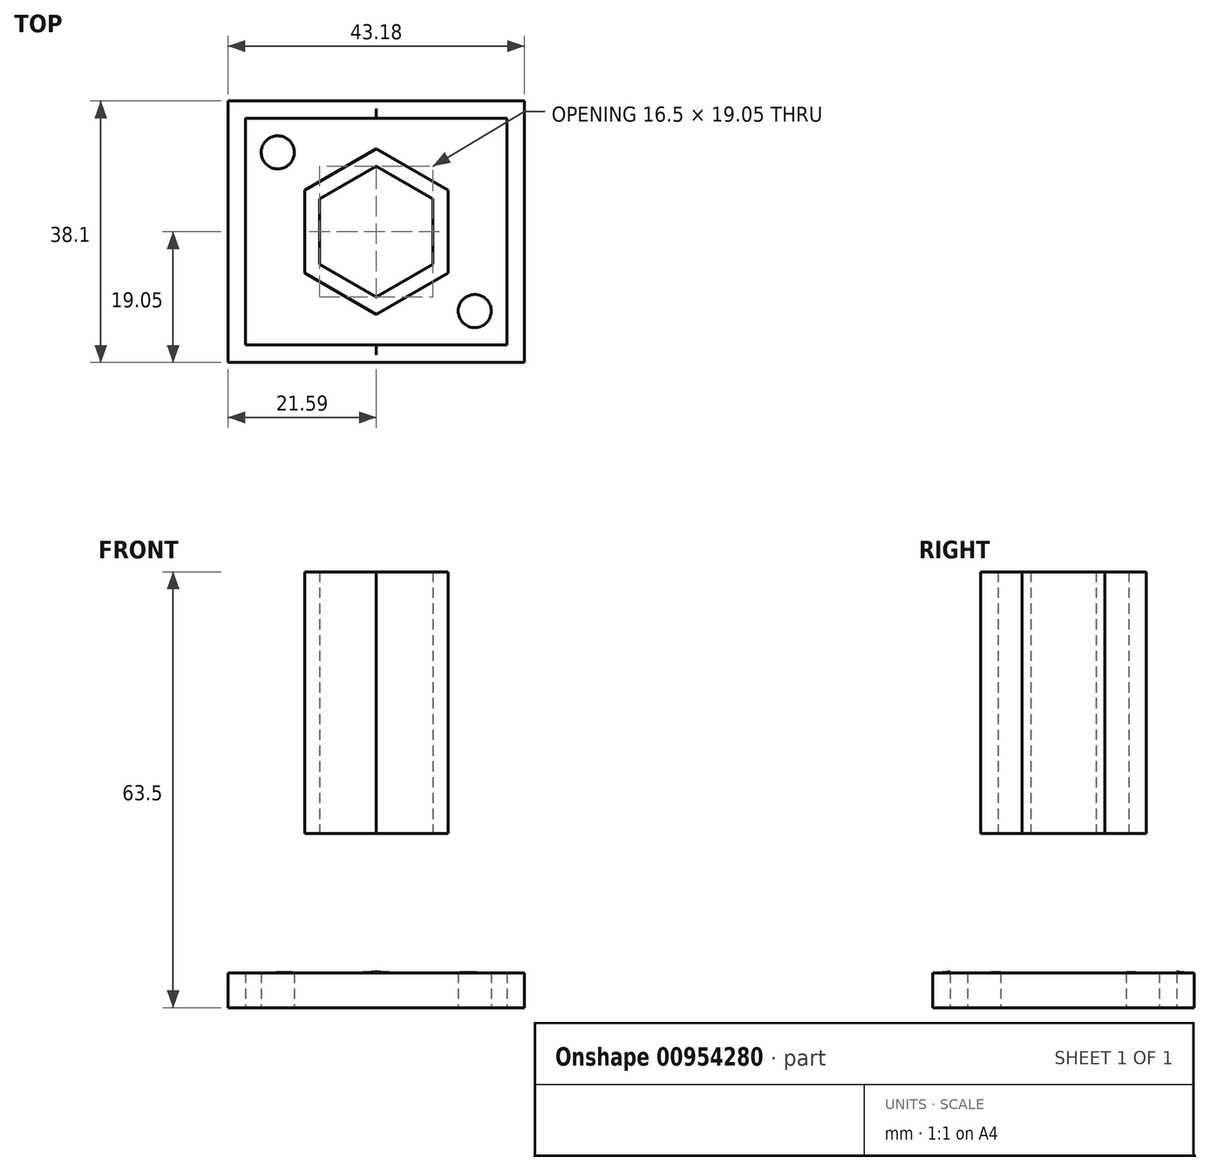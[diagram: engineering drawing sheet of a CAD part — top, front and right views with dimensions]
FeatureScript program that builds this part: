
annotation { "Feature Type Name" : "Feature", "Feature Type Description" : "" }
export const myFeature = defineFeature(function(context is Context, id is Id, definition is map)
    precondition{}
    {
        {
            var Q0;
            Q0=qCreatedBy(makeId("Front.planeOp"),FACE);
            var sketch = newSketch(context, id + "F0", { "sketchPlane" : qUnion([Q0])});
            skLineSegment(sketch, "E0.bottom", {"start": v(-21.59, -11.25) * mm, "end": v(21.59, -11.25) * mm});
            skLineSegment(sketch, "E0.top", {"start": v(-21.59, -16.33) * mm, "end": v(21.59, -16.33) * mm});
            skLineSegment(sketch, "E0.left", {"start": v(-21.59, -11.25) * mm, "end": v(-21.59, -16.33) * mm});
            skLineSegment(sketch, "E0.right", {"start": v(21.59, -11.25) * mm, "end": v(21.59, -16.33) * mm});
            skPoint(sketch, "E0.middle", {"position": v(0, -13.79) * mm});
            skSolve(sketch);
        }
        {
            var Q0;
            Q0=qSketchRegion(id+"F0",true);
            extrude(context, id + "F1", {"entities" : qUnion([Q0]), "endBound" : BoundingType.SYMMETRIC, "depth" : 38.1 * mm, "offsetDistance" : 25.4 * mm});
        }
        {
            var Q0;
            Q0=makeQuery(id+"F1.opExtrude","SWEPT_FACE",FACE,{"disambiguationData":[OSD([sQuery(id+"F0.wireOp",EDGE,"E0.bottom")])]});
            var sketch = newSketch(context, id + "F2", { "sketchPlane" : qUnion([Q0])});
            skCircle(sketch, "E1", {"center": v(0, 0) * mm, "radius": 12.07 * mm, "construction": true});
            skLineSegment(sketch, "E2.0", {"start": v(0, 12.07) * mm, "end": v(10.45, 6.03) * mm});
            skLineSegment(sketch, "E2.1", {"start": v(10.45, 6.03) * mm, "end": v(10.45, -6.03) * mm});
            skLineSegment(sketch, "E2.2", {"start": v(10.45, -6.03) * mm, "end": v(0, -12.07) * mm});
            skLineSegment(sketch, "E2.3", {"start": v(0, -12.06) * mm, "end": v(-10.45, -6.03) * mm});
            skLineSegment(sketch, "E2.4", {"start": v(-10.45, -6.03) * mm, "end": v(-10.45, 6.03) * mm});
            skLineSegment(sketch, "E2.5", {"start": v(-10.45, 6.03) * mm, "end": v(0, 12.07) * mm});
            skCircle(sketch, "E3", {"center": v(0, 0) * mm, "radius": 9.53 * mm, "construction": true});
            skLineSegment(sketch, "E4.0", {"start": v(0, 9.53) * mm, "end": v(8.25, 4.76) * mm});
            skLineSegment(sketch, "E4.1", {"start": v(8.25, 4.76) * mm, "end": v(8.25, -4.76) * mm});
            skLineSegment(sketch, "E4.2", {"start": v(8.25, -4.76) * mm, "end": v(0, -9.53) * mm});
            skLineSegment(sketch, "E4.3", {"start": v(0, -9.53) * mm, "end": v(-8.25, -4.76) * mm});
            skLineSegment(sketch, "E4.4", {"start": v(-8.25, -4.76) * mm, "end": v(-8.25, 4.76) * mm});
            skLineSegment(sketch, "E4.5", {"start": v(-8.25, 4.76) * mm, "end": v(0, 9.52) * mm});
            skSolve(sketch);
        }
        {
            var Q0;
            Q0=qSketchRegion(id+"F2",true);
            extrude(context, id + "F3", {"entities" : qUnion([Q0]), "operationType" : NewBodyOperationType.ADD, "depth" : 58.42 * mm, "offsetDistance" : 25.4 * mm});
        }
        {
            var Q0;
            Q0=makeQuery(id+"F3.opExtrude","CAP_EDGE",EDGE,{"disambiguationData":[OSD([sQuery(id+"F2.wireOp",EDGE,"E2.1")])],"isStart":true});
            var Q1;
            Q1=makeQuery(id+"F3.opExtrude","CAP_EDGE",EDGE,{"disambiguationData":[OSD([sQuery(id+"F2.wireOp",EDGE,"E2.2")])],"isStart":true});
            var Q2;
            Q2=makeQuery(id+"F3.opExtrude","CAP_EDGE",EDGE,{"disambiguationData":[OSD([sQuery(id+"F2.wireOp",EDGE,"E2.3")])],"isStart":true});
            var Q3;
            Q3=makeQuery(id+"F3.opExtrude","CAP_EDGE",EDGE,{"disambiguationData":[OSD([sQuery(id+"F2.wireOp",EDGE,"E2.0")])],"isStart":true});
            var Q4;
            Q4=makeQuery(id+"F3.opExtrude","CAP_EDGE",EDGE,{"disambiguationData":[OSD([sQuery(id+"F2.wireOp",EDGE,"E2.5")])],"isStart":true});
            var Q5;
            Q5=makeQuery(id+"F3.opExtrude","CAP_EDGE",EDGE,{"disambiguationData":[OSD([sQuery(id+"F2.wireOp",EDGE,"E2.4")])],"isStart":true});
            fillet(context, id + "F4", {"entities" : qUnion([Q0, Q1, Q2, Q3, Q4, Q5]), "radius" : 5.08 * mm, "tangentPropagation" : true, "allowEdgeOverflow" : false});
        }
        {
            var Q0;
            Q0=makeQuery(id+"F1.opExtrude","SWEPT_FACE",FACE,{"disambiguationData":[OSD([sQuery(id+"F0.wireOp",EDGE,"E0.top")])]});
            var sketch = newSketch(context, id + "F5", { "sketchPlane" : qUnion([Q0])});
            skLineSegment(sketch, "E5.bottom", {"start": v(-19.05, 16.51) * mm, "end": v(19.05, 16.51) * mm});
            skLineSegment(sketch, "E5.top", {"start": v(-19.05, -16.51) * mm, "end": v(19.05, -16.51) * mm});
            skLineSegment(sketch, "E5.left", {"start": v(-19.05, 16.51) * mm, "end": v(-19.05, -16.51) * mm});
            skLineSegment(sketch, "E5.right", {"start": v(19.05, 16.51) * mm, "end": v(19.05, -16.51) * mm});
            skPoint(sketch, "E5.middle", {"position": v(0, 0) * mm});
            skCircle(sketch, "E6", {"center": v(-14.35, 11.56) * mm, "radius": 2.41 * mm});
            skCircle(sketch, "E7.MirrorC", {"center": v(14.35, 11.56) * mm, "radius": 2.41 * mm});
            skCircle(sketch, "E8.MirrorC", {"center": v(-14.35, -11.56) * mm, "radius": 2.41 * mm});
            skCircle(sketch, "E9.MirrorC", {"center": v(14.35, -11.56) * mm, "radius": 2.41 * mm});
            skSolve(sketch);
        }
        {
            var Q0;
            Q0=makeQuery(id+"F5.imprint","IMPRINT",FACE,{"disambiguationData":[TD([[makeQuery(id+"F5.imprint","IMPRINT",EDGE,{"derivedFrom":sQuery(id+"F5.wireOp",EDGE,"E6")}),1.0]])]});
            var Q1;
            Q1=makeQuery(id+"F5.imprint","IMPRINT",FACE,{"disambiguationData":[TD([[makeQuery(id+"F5.imprint","IMPRINT",EDGE,{"derivedFrom":sQuery(id+"F5.wireOp",EDGE,"E7.MirrorC")}),-1.0]])]});
            var Q2;
            Q2=makeQuery(id+"F5.imprint","IMPRINT",FACE,{"disambiguationData":[TD([[makeQuery(id+"F5.imprint","IMPRINT",EDGE,{"derivedFrom":sQuery(id+"F5.wireOp",EDGE,"E8.MirrorC")}),-1.0]])]});
            var Q3;
            Q3=makeQuery(id+"F5.imprint","IMPRINT",FACE,{"disambiguationData":[TD([[makeQuery(id+"F5.imprint","IMPRINT",EDGE,{"derivedFrom":sQuery(id+"F5.wireOp",EDGE,"E9.MirrorC")}),1.0]])]});
            extrude(context, id + "F6", {"entities" : qUnion([Q0, Q1, Q2, Q3]), "operationType" : NewBodyOperationType.REMOVE, "oppositeDirection" : true, "depth" : 25.4 * mm, "offsetDistance" : 25.4 * mm});
        }
    });
